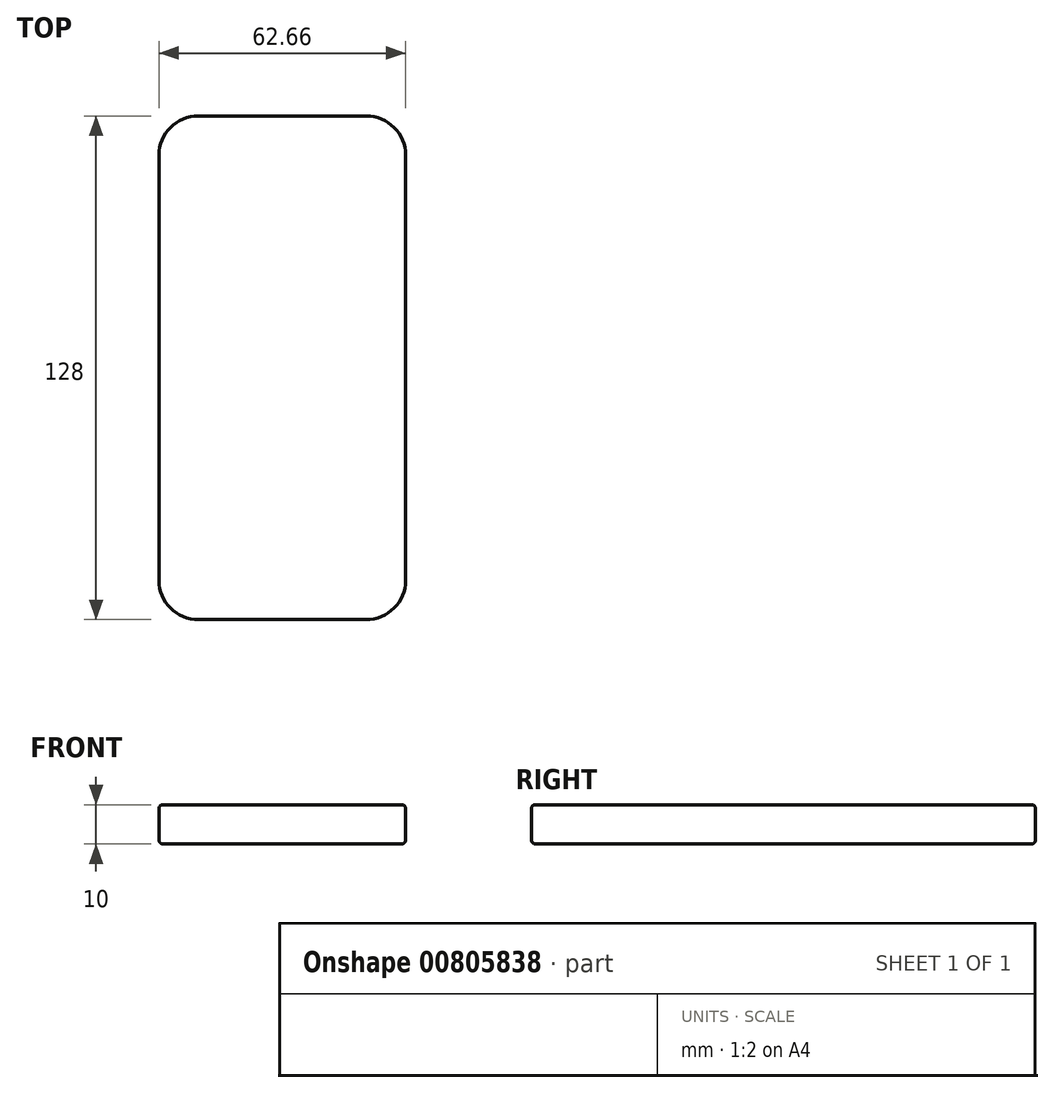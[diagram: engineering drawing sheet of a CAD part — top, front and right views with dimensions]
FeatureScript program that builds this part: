
annotation { "Feature Type Name" : "Feature", "Feature Type Description" : "" }
export const myFeature = defineFeature(function(context is Context, id is Id, definition is map)
    precondition{}
    {
        {
            var Q0;
            Q0=qCreatedBy(makeId("Top.planeOp"),FACE);
            var sketch = newSketch(context, id + "F0", { "sketchPlane" : qUnion([Q0])});
            skLineSegment(sketch, "E0.bottom", {"start": v(31.33, -64) * mm, "end": v(-31.32, -64) * mm});
            skLineSegment(sketch, "E0.top", {"start": v(31.33, 64) * mm, "end": v(-31.32, 64) * mm});
            skLineSegment(sketch, "E0.left", {"start": v(31.33, -64) * mm, "end": v(31.33, 64) * mm});
            skLineSegment(sketch, "E0.right", {"start": v(-31.32, -64) * mm, "end": v(-31.32, 64) * mm});
            skPoint(sketch, "E0.middle", {"position": v(0, 0) * mm});
            skSolve(sketch);
        }
        {
            var Q0;
            Q0 = qSketchRegion(id + "F0", true);
            extrude(context, id + "F1", {"entities" : qUnion([Q0]), "depth" : 10 * mm, "offsetDistance" : 25 * mm});
        }
        {
            var Q0;
            Q0=makeQuery(id+"F1.opExtrude","SWEPT_EDGE",EDGE,{"disambiguationData":[OSD([sQuery(id+"F0.wireOp",EDGE,"E0.top"),sQuery(id+"F0.wireOp",EDGE,"E0.left")])]});
            var Q1;
            Q1=makeQuery(id+"F1.opExtrude","SWEPT_EDGE",EDGE,{"disambiguationData":[OSD([sQuery(id+"F0.wireOp",EDGE,"E0.top"),sQuery(id+"F0.wireOp",EDGE,"E0.right")])]});
            var Q2;
            Q2=makeQuery(id+"F1.opExtrude","SWEPT_EDGE",EDGE,{"disambiguationData":[OSD([sQuery(id+"F0.wireOp",EDGE,"E0.bottom"),sQuery(id+"F0.wireOp",EDGE,"E0.right")])]});
            var Q3;
            Q3=makeQuery(id+"F1.opExtrude","SWEPT_EDGE",EDGE,{"disambiguationData":[OSD([sQuery(id+"F0.wireOp",EDGE,"E0.bottom"),sQuery(id+"F0.wireOp",EDGE,"E0.left")])]});
            fillet(context, id + "F2", {"entities" : qUnion([Q0, Q1, Q2, Q3]), "radius" : 10 * mm, "tangentPropagation" : true, "allowEdgeOverflow" : false});
        }
        {
            var Q0;
            Q0=makeQuery(id+"F1.opExtrude","CAP_FACE",FACE,{"disambiguationData":[OSD([sQuery(id+"F0.wireOp",EDGE,"E0.bottom"),sQuery(id+"F0.wireOp",EDGE,"E0.top"),sQuery(id+"F0.wireOp",EDGE,"E0.left"),sQuery(id+"F0.wireOp",EDGE,"E0.right")])],"isStart":false});
            var Q1;
            Q1=makeQuery(id+"F1.opExtrude","CAP_FACE",FACE,{"disambiguationData":[OSD([sQuery(id+"F0.wireOp",EDGE,"E0.bottom"),sQuery(id+"F0.wireOp",EDGE,"E0.top"),sQuery(id+"F0.wireOp",EDGE,"E0.left"),sQuery(id+"F0.wireOp",EDGE,"E0.right")])],"isStart":true});
            fillet(context, id + "F3", {"entities" : qUnion([Q0, Q1]), "radius" : 1 * mm, "tangentPropagation" : true, "allowEdgeOverflow" : false});
        }
    });
